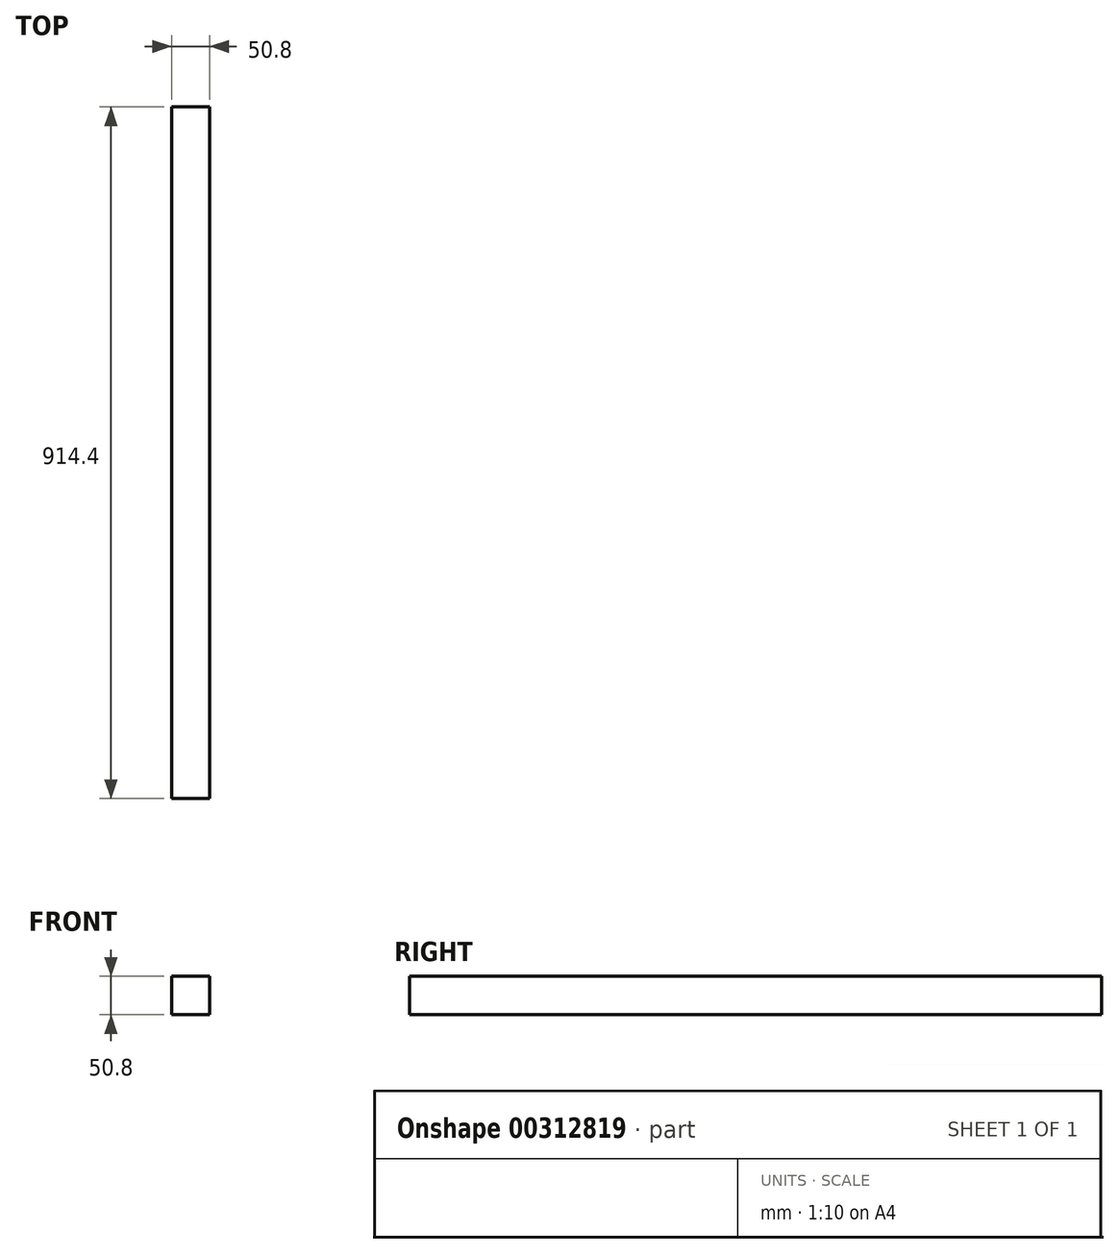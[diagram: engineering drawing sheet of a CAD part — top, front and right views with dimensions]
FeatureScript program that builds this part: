
annotation { "Feature Type Name" : "Feature", "Feature Type Description" : "" }
export const myFeature = defineFeature(function(context is Context, id is Id, definition is map)
    precondition{}
    {
        {
            var Q0;
            Q0=qCreatedBy(makeId("Right.planeOp"),FACE);
            var sketch = newSketch(context, id + "F0", { "sketchPlane" : qUnion([Q0])});
            skLineSegment(sketch, "E0.bottom", {"start": v(-464.94, -52.95) * mm, "end": v(449.46, -52.95) * mm});
            skLineSegment(sketch, "E0.top", {"start": v(-464.94, -103.75) * mm, "end": v(449.46, -103.75) * mm});
            skLineSegment(sketch, "E0.left", {"start": v(-464.94, -52.95) * mm, "end": v(-464.94, -103.75) * mm});
            skLineSegment(sketch, "E0.right", {"start": v(449.46, -52.95) * mm, "end": v(449.46, -103.75) * mm});
            skSolve(sketch);
        }
        {
            var Q0;
            Q0 = qSketchRegion(id + "F0", true);
            extrude(context, id + "F1", {"entities" : qUnion([Q0]), "depth" : 50.8 * mm});
        }
    });
